# Revit family: PRD_FrankeWS_Snks_WorkroomSink_SIRW775
name_source: partatom
category: Plumbing Fixtures
revit_build: Autodesk Revit 2018 (Build: 20190510_1515(x64)
units: mm (PartAtom-declared; Revit-internal decimal feet)

## family parameters
Cut with Voids When Loaded = Yes
Host = Face
OmniClass Number = 23.45.05.14.14.17
OmniClass Title = Plaster Sinks
Part Type = Normal
Room Calculation Point = No
Round Connector Dimension = Use Diameter
Shared = Yes

## types (1)
- SIRW775
    AssetType = Fixed
    BIMObjectName = PRD_AR_Sinks_WorkroomSink_SIRW775
    BowlDepth = 560.00 mm
    BowlFinish = High polished
    BowlHeight = 283.00 mm
    BowlPosition = Center
    BowlWidth = 1960.00 mm
    Brushes = Without brushes
    Category = Pr_40_20_96_81, Sinks
    Color = Alpine white
    Default Elevation = 0 mm  [stored 0 ft]
    Description = Workroom sink made of MIRANIT resin-bonded mineral material with pore-free smooth surface (temperature-resistant up to 80 °C). Basin without tap landing. Large inner radii, bottom of basin with 2° slope. Alpine white colour. Welded substructure frame, powder-coated in basin colour, adjustable base feet. Mounting material included. Drain with under-screwed waste unit including removable sludge bucket, DN 40 overflow at waste unit and DN 25 waste outlet spigot made of stainless steel. Waste unit with DN 40 ball cock completely fitted with tubes. Waste unit rotatable by 90°.
    DiameterNominal = 40  [stored 0.131234 ft]
    DrainSize = 40 mm  [stored 0.131234 ft]
    DrainerOrStorage = No
    DurationUnit = year
    Features = resin-bonded mineral material with pore-free smooth surface
    Finish = Coated
    Grid = No
    GrossWeight = 169.00 kg
    IfcExportAs = IfcSanitaryTerminalType
    IfcExportType = SINK
    IntegralAccessories = incl. mounting material
    Manufacturer = KWC Group AG
    ManufacturerName = KWC Group AG
    ManufacturerURL = www.kwc.com
    Material = mineral material
    MaterialCode = Miranit
    Model = SIRW775
    ModelNumber = 2000102725
    ModelReference = SIRW775
    Mounting = Pedestal
    MountingOffset = 0 mm  [stored 0 ft]
    NBSDescription = Sinks
    NBSReference = 45-35-70/344
    Name = Workroom Sink SIRW775
    NetWeight = 160.55 kg
    NominalDepth = 600 mm
    NominalHeight = 800 mm  [stored 2.62467 ft]
    NominalWidth = 2000 mm  [stored 6.56168 ft]
    NumberOfWasteHoles = 1
    OutletSize = DN 40
    Overflow = No
    ProductInformation = https://pim.kwc.com
    RearUpstand = No
    Shape = Cuboid
    SinkMaterial = PRD_AR_ResinBondedMaterial_White
    SinkType = Plaster
    Size = 2000 x 300/800 x 600 mm (W x H x D)
    Spillway = No
    Splashback = No
    StandMaterial = PRD_AR_Black
    StrainerMaterial = PRD_AR_StainlessSteel_SatinFinished
    Sump = Yes
    SumpBasket = Included
    TapLedge = No
    TypeOfMounting = Wall and floor mounting
    TypeOfUtilitySink = Cleaner sink
    URL = www.kwc.com
    Uniclass2015Code = Pr_40_20_96_81
    Uniclass2015Title = Sinks
    Uniclass2015Version = Products v1.17
    UpperEdgeOfBasinHeight = 800.00 mm
    Version = 1
    WarrantyDurationUnit = year
    WashRiffle = No
    WasteHolePosition = Center back
    WasteHoleProjection = 200.00 mm

note: [stored X ft] marks values corroborated as IEEE doubles in the binary element streams (Revit-internal decimal feet)

## geometry (parser evidence)
native form markers: Sweep x5
no freeform markers — native parametric forms only
